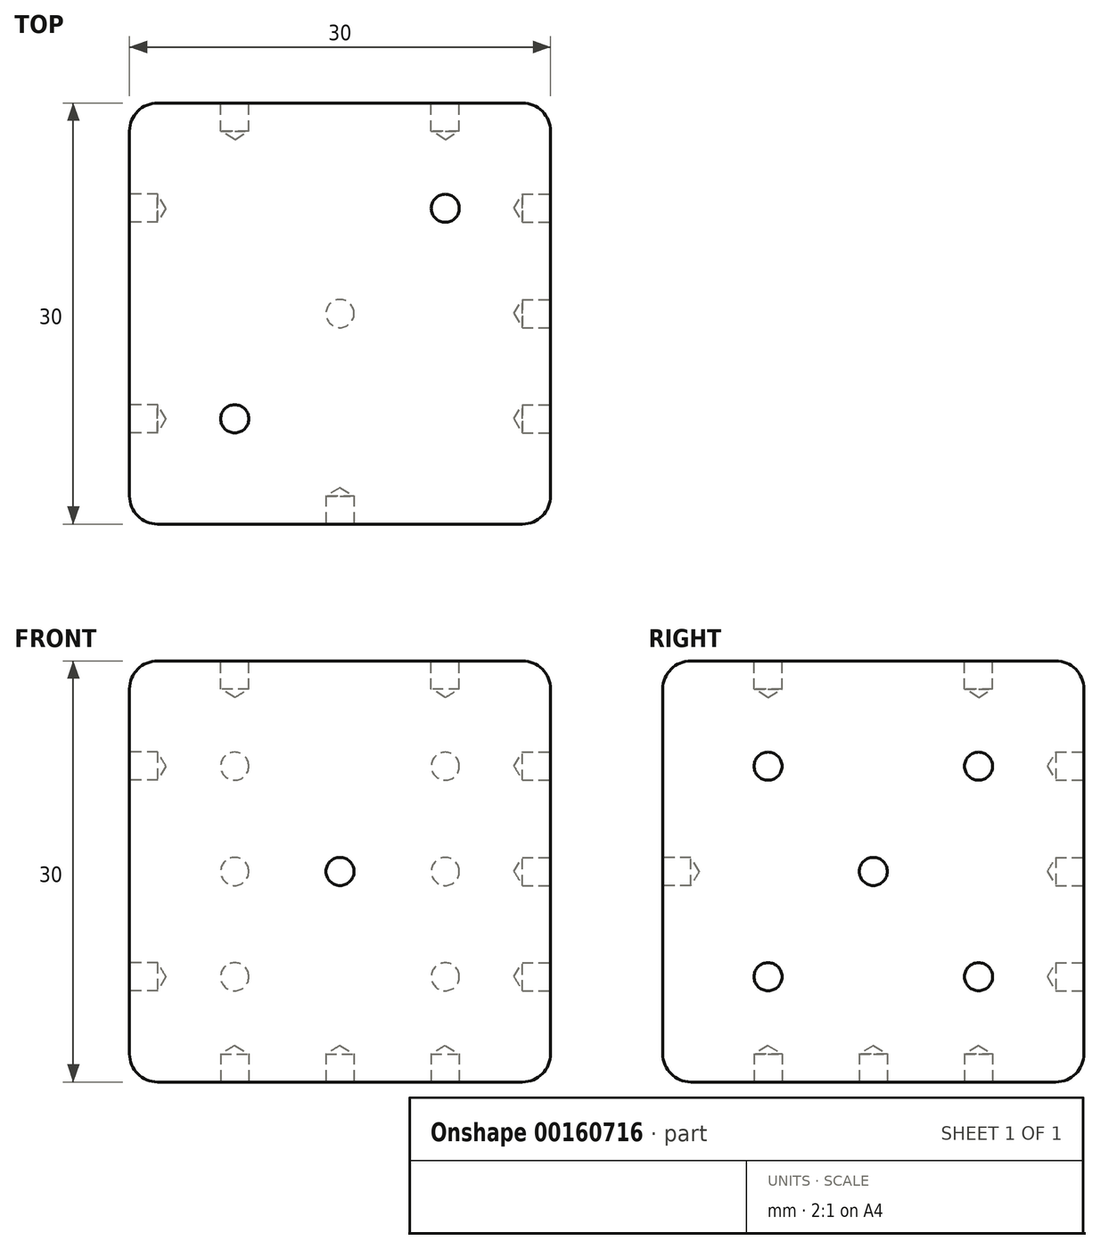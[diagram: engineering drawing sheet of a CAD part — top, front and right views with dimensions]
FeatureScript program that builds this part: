
annotation { "Feature Type Name" : "Feature", "Feature Type Description" : "" }
export const myFeature = defineFeature(function(context is Context, id is Id, definition is map)
    precondition{}
    {
        {
            var Q0;
            Q0=qCreatedBy(makeId("Front.planeOp"),FACE);
            var sketch = newSketch(context, id + "F0", { "sketchPlane" : qUnion([Q0])});
            skLineSegment(sketch, "E0.bottom", {"start": v(-15, 15) * mm, "end": v(15, 15) * mm});
            skLineSegment(sketch, "E0.top", {"start": v(-15, -15) * mm, "end": v(15, -15) * mm});
            skLineSegment(sketch, "E0.left", {"start": v(-15, 15) * mm, "end": v(-15, -15) * mm});
            skLineSegment(sketch, "E0.right", {"start": v(15, 15) * mm, "end": v(15, -15) * mm});
            skPoint(sketch, "E0.middle", {"position": v(0, 0) * mm});
            skSolve(sketch);
        }
        {
            var Q0;
            Q0 = qSketchRegion(id + "F0", true);
            extrude(context, id + "F1", {"entities" : qUnion([Q0]), "depth" : 15 * mm});
        }
        {
            var Q0;
            Q0=makeQuery(id+"F1.opExtrude","CAP_FACE",FACE,{"disambiguationData":[OSD([sQuery(id+"F0.wireOp",EDGE,"E0.bottom"),sQuery(id+"F0.wireOp",EDGE,"E0.top"),sQuery(id+"F0.wireOp",EDGE,"E0.left"),sQuery(id+"F0.wireOp",EDGE,"E0.right")])],"isStart":true});
            extrude(context, id + "F2", {"entities" : qUnion([Q0]), "operationType" : NewBodyOperationType.ADD, "depth" : 15 * mm});
        }
        {
            var Q0;
            Q0=makeQuery(id+"F1.opExtrude","CAP_FACE",FACE,{"disambiguationData":[OSD([sQuery(id+"F0.wireOp",EDGE,"E0.bottom"),sQuery(id+"F0.wireOp",EDGE,"E0.top"),sQuery(id+"F0.wireOp",EDGE,"E0.left"),sQuery(id+"F0.wireOp",EDGE,"E0.right")])],"isStart":false});
            var sketch = newSketch(context, id + "F3", { "sketchPlane" : qUnion([Q0])});
            skPoint(sketch, "E1", {"position": v(0, 0) * mm});
            skSolve(sketch);
        }
        {
            var Q0;
            Q0=sQuery(id+"F3.wireOp",VERTEX,"E1");
            var Q1;
            Q1=makeQuery(id+"F1.opExtrude","SWEPT_BODY",BODY,{"disambiguationData":[OSD([sQuery(id+"F0.wireOp",EDGE,"E0.bottom"),sQuery(id+"F0.wireOp",EDGE,"E0.top"),sQuery(id+"F0.wireOp",EDGE,"E0.left"),sQuery(id+"F0.wireOp",EDGE,"E0.right")])]});
            hole(context, id + "F4", {"style" : HoleStyle.SIMPLE, "endStyle" : HoleEndStyle.BLIND, "holeDiameter" : 2 * mm, "holeDepth" : 2 * mm, "locations" : qUnion([Q0]), "scope" : qUnion([Q1])});
        }
        {
            var Q0;
            {var subQ0=sQuery(id+"F0.wireOp",EDGE,"E0.left");Q0=makeQuery(id+"F2.boolean.opBoolean","MERGE",FACE,{"derivedFrom":[makeQuery(id+"F1.opExtrude","SWEPT_FACE",FACE,{"disambiguationData":[OSD([subQ0])]}),makeQuery(id+"F2.opExtrude","SWEPT_FACE",FACE,{"disambiguationData":[OSD([subQ0])]})]});}
            var sketch = newSketch(context, id + "F5", { "sketchPlane" : qUnion([Q0])});
            skLineSegment(sketch, "E2", {"start": v(0, 0) * mm, "end": v(-15, 15) * mm});
            skLineSegment(sketch, "E3", {"start": v(0, 0) * mm, "end": v(15, -15) * mm});
            skLineSegment(sketch, "E4", {"start": v(0, 0) * mm, "end": v(15, 15) * mm});
            skLineSegment(sketch, "E5", {"start": v(0, 0) * mm, "end": v(-15, -15) * mm});
            skLineSegment(sketch, "E6", {"start": v(-15, 0) * mm, "end": v(0, 15) * mm});
            skLineSegment(sketch, "E7", {"start": v(-15, 0) * mm, "end": v(0, -15) * mm});
            skLineSegment(sketch, "E8", {"start": v(0, -15) * mm, "end": v(15, 0) * mm});
            skLineSegment(sketch, "E9", {"start": v(0, 15) * mm, "end": v(15, 0) * mm});
            skLineSegment(sketch, "E10", {"start": v(-7.5, 7.5) * mm, "end": v(15, 7.5) * mm});
            skPoint(sketch, "E10.endSnap0", {"position": v(7.5, 7.5) * mm});
            skLineSegment(sketch, "E11", {"start": v(-7.5, 7.5) * mm, "end": v(-15, 7.5) * mm});
            skLineSegment(sketch, "E12", {"start": v(-7.5, 7.5) * mm, "end": v(-7.5, -15) * mm});
            skLineSegment(sketch, "E13", {"start": v(7.5, 7.5) * mm, "end": v(7.5, -15) * mm});
            skLineSegment(sketch, "E14", {"start": v(-7.5, 7.5) * mm, "end": v(-7.5, 15) * mm});
            skLineSegment(sketch, "E15", {"start": v(7.5, 7.5) * mm, "end": v(7.5, 15) * mm});
            skLineSegment(sketch, "E16", {"start": v(-7.5, -7.5) * mm, "end": v(15, -7.5) * mm});
            skLineSegment(sketch, "E17", {"start": v(-7.5, -7.5) * mm, "end": v(-15, -7.5) * mm});
            skLineSegment(sketch, "E18", {"start": v(-15, 7.5) * mm, "end": v(-7.5, 15) * mm});
            skLineSegment(sketch, "E19", {"start": v(15, 7.5) * mm, "end": v(7.5, 15) * mm});
            skLineSegment(sketch, "E20", {"start": v(7.5, -15) * mm, "end": v(15, -7.5) * mm});
            skLineSegment(sketch, "E21", {"start": v(-7.5, -15) * mm, "end": v(-15, -7.5) * mm});
            skPoint(sketch, "E22", {"position": v(-11.25, -11.25) * mm});
            skPoint(sketch, "E23", {"position": v(11.25, -11.25) * mm});
            skPoint(sketch, "E24", {"position": v(11.25, 11.25) * mm});
            skPoint(sketch, "E25", {"position": v(-11.25, 11.25) * mm});
            skPoint(sketch, "E26", {"position": v(-7.5, 7.5) * mm});
            skPoint(sketch, "E27", {"position": v(-7.5, -7.5) * mm});
            skPoint(sketch, "E28", {"position": v(7.5, -7.5) * mm});
            skSolve(sketch);
        }
        {
            var Q0;
            {var subQ0=sQuery(id+"F0.wireOp",EDGE,"E0.bottom");Q0=makeQuery(id+"F2.boolean.opBoolean","MERGE",FACE,{"derivedFrom":[makeQuery(id+"F1.opExtrude","SWEPT_FACE",FACE,{"disambiguationData":[OSD([subQ0])]}),makeQuery(id+"F2.opExtrude","SWEPT_FACE",FACE,{"disambiguationData":[OSD([subQ0])]})]});}
            var sketch = newSketch(context, id + "F6", { "sketchPlane" : qUnion([Q0])});
            skLineSegment(sketch, "E29", {"start": v(-15, -15) * mm, "end": v(15, 15) * mm});
            skLineSegment(sketch, "E30", {"start": v(-15, 0) * mm, "end": v(0, -15) * mm});
            skLineSegment(sketch, "E31", {"start": v(0, 15) * mm, "end": v(15, 0) * mm});
            skPoint(sketch, "E32", {"position": v(7.5, 7.5) * mm});
            skPoint(sketch, "E33", {"position": v(-7.5, -7.5) * mm});
            skSolve(sketch);
        }
        {
            var Q0;
            Q0=sQuery(id+"F6.wireOp",VERTEX,"E33");
            var Q1;
            Q1=sQuery(id+"F6.wireOp",VERTEX,"E32");
            var Q2;
            Q2=makeQuery(id+"F1.opExtrude","SWEPT_BODY",BODY,{"disambiguationData":[OSD([sQuery(id+"F0.wireOp",EDGE,"E0.bottom"),sQuery(id+"F0.wireOp",EDGE,"E0.top"),sQuery(id+"F0.wireOp",EDGE,"E0.left"),sQuery(id+"F0.wireOp",EDGE,"E0.right")])]});
            hole(context, id + "F7", {"style" : HoleStyle.SIMPLE, "endStyle" : HoleEndStyle.BLIND, "holeDiameter" : 2 * mm, "holeDepth" : 2 * mm, "locations" : qUnion([Q0, Q1]), "scope" : qUnion([Q2])});
        }
        {
            var Q0;
            Q0=makeQuery(id+"F2.opExtrude","CAP_FACE",FACE,{"disambiguationData":[OSD([sQuery(id+"F0.wireOp",EDGE,"E0.bottom"),sQuery(id+"F0.wireOp",EDGE,"E0.top"),sQuery(id+"F0.wireOp",EDGE,"E0.left"),sQuery(id+"F0.wireOp",EDGE,"E0.right")])],"isStart":false});
            var sketch = newSketch(context, id + "F8", { "sketchPlane" : qUnion([Q0])});
            skLineSegment(sketch, "E34", {"start": v(-15, 0) * mm, "end": v(15, 0) * mm});
            skLineSegment(sketch, "E35", {"start": v(0, 15) * mm, "end": v(15, 0) * mm});
            skLineSegment(sketch, "E36", {"start": v(0, 15) * mm, "end": v(-15, 0) * mm});
            skLineSegment(sketch, "E37", {"start": v(-15, 15) * mm, "end": v(15, -15) * mm});
            skLineSegment(sketch, "E38", {"start": v(-15, -15) * mm, "end": v(15, 15) * mm});
            skPoint(sketch, "E39", {"position": v(-7.5, 7.5) * mm});
            skLineSegment(sketch, "E40", {"start": v(-15, 0) * mm, "end": v(0, -15) * mm});
            skLineSegment(sketch, "E41", {"start": v(15, 0) * mm, "end": v(0, -15) * mm});
            skLineSegment(sketch, "E42", {"start": v(7.5, 7.5) * mm, "end": v(7.5, -15) * mm});
            skLineSegment(sketch, "E43", {"start": v(-7.5, 7.5) * mm, "end": v(-7.5, -15) * mm});
            skLineSegment(sketch, "E44", {"start": v(-7.5, 7.5) * mm, "end": v(-7.5, 15) * mm});
            skLineSegment(sketch, "E45", {"start": v(7.5, 7.5) * mm, "end": v(7.5, 15) * mm});
            skPoint(sketch, "E46", {"position": v(7.5, 7.5) * mm});
            skPoint(sketch, "E47", {"position": v(7.5, -7.5) * mm});
            skPoint(sketch, "E48", {"position": v(-7.5, -7.5) * mm});
            skLineSegment(sketch, "E49", {"start": v(-15, 15) * mm, "end": v(0, -15) * mm});
            skLineSegment(sketch, "E50", {"start": v(0, -15) * mm, "end": v(15, 15) * mm});
            skPoint(sketch, "E51", {"position": v(-7.5, 0) * mm});
            skPoint(sketch, "E52", {"position": v(7.5, 0) * mm});
            skSolve(sketch);
        }
        {
            var Q0;
            Q0=sQuery(id+"F8.wireOp",VERTEX,"E39");
            var Q1;
            Q1=sQuery(id+"F8.wireOp",VERTEX,"E51");
            var Q2;
            Q2=sQuery(id+"F8.wireOp",VERTEX,"E48");
            var Q3;
            Q3=sQuery(id+"F8.wireOp",VERTEX,"E47");
            var Q4;
            Q4=sQuery(id+"F8.wireOp",VERTEX,"E52");
            var Q5;
            Q5=sQuery(id+"F8.wireOp",VERTEX,"E46");
            var Q6;
            Q6=makeQuery(id+"F1.opExtrude","SWEPT_BODY",BODY,{"disambiguationData":[OSD([sQuery(id+"F0.wireOp",EDGE,"E0.bottom"),sQuery(id+"F0.wireOp",EDGE,"E0.top"),sQuery(id+"F0.wireOp",EDGE,"E0.left"),sQuery(id+"F0.wireOp",EDGE,"E0.right")])]});
            hole(context, id + "F9", {"style" : HoleStyle.SIMPLE, "endStyle" : HoleEndStyle.BLIND, "holeDiameter" : 2 * mm, "holeDepth" : 2 * mm, "locations" : qUnion([Q0, Q1, Q2, Q3, Q4, Q5]), "scope" : qUnion([Q6])});
        }
        {
            var Q0;
            {var subQ0=sQuery(id+"F0.wireOp",EDGE,"E0.top");Q0=makeQuery(id+"F2.boolean.opBoolean","MERGE",FACE,{"derivedFrom":[makeQuery(id+"F1.opExtrude","SWEPT_FACE",FACE,{"disambiguationData":[OSD([subQ0])]}),makeQuery(id+"F2.opExtrude","SWEPT_FACE",FACE,{"disambiguationData":[OSD([subQ0])]})]});}
            var sketch = newSketch(context, id + "F10", { "sketchPlane" : qUnion([Q0])});
            skLineSegment(sketch, "E53", {"start": v(15, -15) * mm, "end": v(-15, 15) * mm});
            skLineSegment(sketch, "E54", {"start": v(0, -15) * mm, "end": v(15, 0) * mm});
            skLineSegment(sketch, "E55", {"start": v(-15, 0) * mm, "end": v(0, 15) * mm});
            skPoint(sketch, "E56", {"position": v(-7.5, 7.5) * mm});
            skPoint(sketch, "E57", {"position": v(7.5, -7.5) * mm});
            skPoint(sketch, "E58", {"position": v(0, 0) * mm});
            skSolve(sketch);
        }
        {
            var Q0;
            Q0=sQuery(id+"F10.wireOp",VERTEX,"E57");
            var Q1;
            Q1=sQuery(id+"F10.wireOp",VERTEX,"E58");
            var Q2;
            Q2=sQuery(id+"F10.wireOp",VERTEX,"E56");
            var Q3;
            Q3=makeQuery(id+"F1.opExtrude","SWEPT_BODY",BODY,{"disambiguationData":[OSD([sQuery(id+"F0.wireOp",EDGE,"E0.bottom"),sQuery(id+"F0.wireOp",EDGE,"E0.top"),sQuery(id+"F0.wireOp",EDGE,"E0.left"),sQuery(id+"F0.wireOp",EDGE,"E0.right")])]});
            hole(context, id + "F11", {"style" : HoleStyle.SIMPLE, "endStyle" : HoleEndStyle.BLIND, "holeDiameter" : 2 * mm, "holeDepth" : 2 * mm, "locations" : qUnion([Q0, Q1, Q2]), "scope" : qUnion([Q3])});
        }
        {
            var Q0;
            {var subQ0=sQuery(id+"F0.wireOp",EDGE,"E0.right");Q0=makeQuery(id+"F2.boolean.opBoolean","MERGE",FACE,{"derivedFrom":[makeQuery(id+"F1.opExtrude","SWEPT_FACE",FACE,{"disambiguationData":[OSD([subQ0])]}),makeQuery(id+"F2.opExtrude","SWEPT_FACE",FACE,{"disambiguationData":[OSD([subQ0])]})]});}
            var sketch = newSketch(context, id + "F12", { "sketchPlane" : qUnion([Q0])});
            skLineSegment(sketch, "E59", {"start": v(-15, 15) * mm, "end": v(15, -15) * mm});
            skLineSegment(sketch, "E60", {"start": v(15, 15) * mm, "end": v(-15, -15) * mm});
            skLineSegment(sketch, "E61", {"start": v(15, 0) * mm, "end": v(0, -15) * mm});
            skLineSegment(sketch, "E62", {"start": v(0, -15) * mm, "end": v(-15, 0) * mm});
            skLineSegment(sketch, "E63", {"start": v(-15, 0) * mm, "end": v(0, 15) * mm});
            skLineSegment(sketch, "E64", {"start": v(0, 15) * mm, "end": v(15, 0) * mm});
            skLineSegment(sketch, "E65", {"start": v(-15, 15) * mm, "end": v(0, -15) * mm});
            skLineSegment(sketch, "E66", {"start": v(0, -15) * mm, "end": v(15, 15) * mm});
            skLineSegment(sketch, "E67", {"start": v(15, 15) * mm, "end": v(-15, 0) * mm});
            skLineSegment(sketch, "E68", {"start": v(-15, 0) * mm, "end": v(15, -15) * mm});
            skLineSegment(sketch, "E69", {"start": v(15, -15) * mm, "end": v(0, 15) * mm});
            skLineSegment(sketch, "E70", {"start": v(0, 15) * mm, "end": v(-15, -15) * mm});
            skLineSegment(sketch, "E71", {"start": v(15, 0) * mm, "end": v(-15, 15) * mm});
            skLineSegment(sketch, "E72", {"start": v(-15, -15) * mm, "end": v(15, 0) * mm});
            skLineSegment(sketch, "E73", {"start": v(-7.5, 7.5) * mm, "end": v(-7.5, 15) * mm});
            skLineSegment(sketch, "E74", {"start": v(-7.5, 15) * mm, "end": v(-15, 0) * mm});
            skLineSegment(sketch, "E75", {"start": v(7.5, 7.5) * mm, "end": v(7.5, 15) * mm});
            skLineSegment(sketch, "E76", {"start": v(7.5, 15) * mm, "end": v(15, 0) * mm});
            skLineSegment(sketch, "E77", {"start": v(7.5, -7.5) * mm, "end": v(7.5, -15) * mm});
            skLineSegment(sketch, "E78", {"start": v(7.5, -15) * mm, "end": v(15, 0) * mm});
            skLineSegment(sketch, "E79", {"start": v(-7.5, -7.5) * mm, "end": v(-7.5, -15) * mm});
            skLineSegment(sketch, "E80", {"start": v(-7.5, -15) * mm, "end": v(-15, 0) * mm});
            skLineSegment(sketch, "E81", {"start": v(-7.5, 7.5) * mm, "end": v(15, 7.5) * mm});
            skLineSegment(sketch, "E82", {"start": v(-7.5, 7.5) * mm, "end": v(-15, 7.5) * mm});
            skLineSegment(sketch, "E83", {"start": v(-7.5, -7.5) * mm, "end": v(15, -7.5) * mm});
            skLineSegment(sketch, "E84", {"start": v(-7.5, -7.5) * mm, "end": v(-15, -7.5) * mm});
            skLineSegment(sketch, "E85", {"start": v(-15, 7.5) * mm, "end": v(-7.5, 15) * mm});
            skLineSegment(sketch, "E86", {"start": v(7.5, 15) * mm, "end": v(15, 7.5) * mm});
            skLineSegment(sketch, "E87", {"start": v(15, -7.5) * mm, "end": v(7.5, -15) * mm});
            skLineSegment(sketch, "E88", {"start": v(-7.5, -15) * mm, "end": v(-15, -7.5) * mm});
            skPoint(sketch, "E89", {"position": v(-11.25, -11.25) * mm});
            skPoint(sketch, "E90", {"position": v(-11.25, 11.25) * mm});
            skPoint(sketch, "E91", {"position": v(11.25, 11.25) * mm});
            skPoint(sketch, "E92", {"position": v(11.25, -11.25) * mm});
            skPoint(sketch, "E93", {"position": v(0, 0) * mm});
            skPoint(sketch, "E94", {"position": v(-7.5, 7.5) * mm});
            skPoint(sketch, "E95", {"position": v(7.5, 7.5) * mm});
            skPoint(sketch, "E96", {"position": v(7.5, -7.5) * mm});
            skPoint(sketch, "E97", {"position": v(-7.5, -7.5) * mm});
            skSolve(sketch);
        }
        {
            var Q0;
            {var subQ0=sQuery(id+"F0.wireOp",EDGE,"E0.right");var subQ1=sQuery(id+"F0.wireOp",EDGE,"E0.bottom");Q0=makeQuery(id+"F2.boolean.opBoolean","MERGE",EDGE,{"derivedFrom":[makeQuery(id+"F1.opExtrude","SWEPT_EDGE",EDGE,{"disambiguationData":[OSD([subQ1,subQ0])]}),makeQuery(id+"F2.opExtrude","SWEPT_EDGE",EDGE,{"disambiguationData":[OSD([subQ1,subQ0])]})]});}
            var Q1;
            Q1=makeQuery(id+"F1.opExtrude","CAP_EDGE",EDGE,{"disambiguationData":[OSD([sQuery(id+"F0.wireOp",EDGE,"E0.bottom")])],"isStart":false});
            var Q2;
            Q2=makeQuery(id+"F1.opExtrude","CAP_EDGE",EDGE,{"disambiguationData":[OSD([sQuery(id+"F0.wireOp",EDGE,"E0.right")])],"isStart":false});
            var Q3;
            {var subQ0=sQuery(id+"F0.wireOp",EDGE,"E0.right");var subQ1=sQuery(id+"F0.wireOp",EDGE,"E0.top");Q3=makeQuery(id+"F2.boolean.opBoolean","MERGE",EDGE,{"derivedFrom":[makeQuery(id+"F1.opExtrude","SWEPT_EDGE",EDGE,{"disambiguationData":[OSD([subQ1,subQ0])]}),makeQuery(id+"F2.opExtrude","SWEPT_EDGE",EDGE,{"disambiguationData":[OSD([subQ1,subQ0])]})]});}
            var Q4;
            Q4=makeQuery(id+"F1.opExtrude","CAP_EDGE",EDGE,{"disambiguationData":[OSD([sQuery(id+"F0.wireOp",EDGE,"E0.top")])],"isStart":false});
            var Q5;
            Q5=makeQuery(id+"F1.opExtrude","CAP_EDGE",EDGE,{"disambiguationData":[OSD([sQuery(id+"F0.wireOp",EDGE,"E0.left")])],"isStart":false});
            var Q6;
            {var subQ0=sQuery(id+"F0.wireOp",EDGE,"E0.left");var subQ1=sQuery(id+"F0.wireOp",EDGE,"E0.top");Q6=makeQuery(id+"F2.boolean.opBoolean","MERGE",EDGE,{"derivedFrom":[makeQuery(id+"F1.opExtrude","SWEPT_EDGE",EDGE,{"disambiguationData":[OSD([subQ1,subQ0])]}),makeQuery(id+"F2.opExtrude","SWEPT_EDGE",EDGE,{"disambiguationData":[OSD([subQ1,subQ0])]})]});}
            var Q7;
            {var subQ0=sQuery(id+"F0.wireOp",EDGE,"E0.left");var subQ1=sQuery(id+"F0.wireOp",EDGE,"E0.bottom");Q7=makeQuery(id+"F2.boolean.opBoolean","MERGE",EDGE,{"derivedFrom":[makeQuery(id+"F1.opExtrude","SWEPT_EDGE",EDGE,{"disambiguationData":[OSD([subQ1,subQ0])]}),makeQuery(id+"F2.opExtrude","SWEPT_EDGE",EDGE,{"disambiguationData":[OSD([subQ1,subQ0])]})]});}
            var Q8;
            Q8=makeQuery(id+"F2.opExtrude","CAP_EDGE",EDGE,{"disambiguationData":[OSD([sQuery(id+"F0.wireOp",EDGE,"E0.left")])],"isStart":false});
            var Q9;
            Q9=makeQuery(id+"F2.opExtrude","CAP_EDGE",EDGE,{"disambiguationData":[OSD([sQuery(id+"F0.wireOp",EDGE,"E0.bottom")])],"isStart":false});
            var Q10;
            Q10=makeQuery(id+"F2.opExtrude","CAP_EDGE",EDGE,{"disambiguationData":[OSD([sQuery(id+"F0.wireOp",EDGE,"E0.top")])],"isStart":false});
            var Q11;
            Q11=makeQuery(id+"F2.opExtrude","CAP_EDGE",EDGE,{"disambiguationData":[OSD([sQuery(id+"F0.wireOp",EDGE,"E0.right")])],"isStart":false});
            fillet(context, id + "F13", {"entities" : qUnion([Q0, Q1, Q2, Q3, Q4, Q5, Q6, Q7, Q8, Q9, Q10, Q11]), "radius" : 2 * mm, "tangentPropagation" : true, "allowEdgeOverflow" : false});
        }
        {
            var Q0;
            Q0=sQuery(id+"F12.wireOp",VERTEX,"E94");
            var Q1;
            Q1=sQuery(id+"F12.wireOp",VERTEX,"E95");
            var Q2;
            Q2=sQuery(id+"F12.wireOp",VERTEX,"E96");
            var Q3;
            Q3=sQuery(id+"F12.wireOp",VERTEX,"E97");
            var Q4;
            Q4=sQuery(id+"F12.wireOp",VERTEX,"E93");
            var Q5;
            Q5=makeQuery(id+"F1.opExtrude","SWEPT_BODY",BODY,{"disambiguationData":[OSD([sQuery(id+"F0.wireOp",EDGE,"E0.bottom"),sQuery(id+"F0.wireOp",EDGE,"E0.top"),sQuery(id+"F0.wireOp",EDGE,"E0.left"),sQuery(id+"F0.wireOp",EDGE,"E0.right")])]});
            hole(context, id + "F14", {"style" : HoleStyle.SIMPLE, "endStyle" : HoleEndStyle.BLIND, "holeDiameter" : 2 * mm, "holeDepth" : 2 * mm, "locations" : qUnion([Q0, Q1, Q2, Q3, Q4]), "scope" : qUnion([Q5])});
        }
        {
            var Q0;
            Q0=sQuery(id+"F5.wireOp",VERTEX,"E28");
            var Q1;
            Q1=sQuery(id+"F5.wireOp",VERTEX,"E27");
            var Q2;
            Q2=sQuery(id+"F5.wireOp",VERTEX,"E26");
            var Q3;
            Q3=sQuery(id+"F5.wireOp",VERTEX,"E10.endSnap0");
            var Q4;
            Q4=makeQuery(id+"F1.opExtrude","SWEPT_BODY",BODY,{"disambiguationData":[OSD([sQuery(id+"F0.wireOp",EDGE,"E0.bottom"),sQuery(id+"F0.wireOp",EDGE,"E0.top"),sQuery(id+"F0.wireOp",EDGE,"E0.left"),sQuery(id+"F0.wireOp",EDGE,"E0.right")])]});
            hole(context, id + "F15", {"style" : HoleStyle.SIMPLE, "endStyle" : HoleEndStyle.BLIND, "holeDiameter" : 2 * mm, "holeDepth" : 2 * mm, "locations" : qUnion([Q0, Q1, Q2, Q3]), "scope" : qUnion([Q4])});
        }
    });
